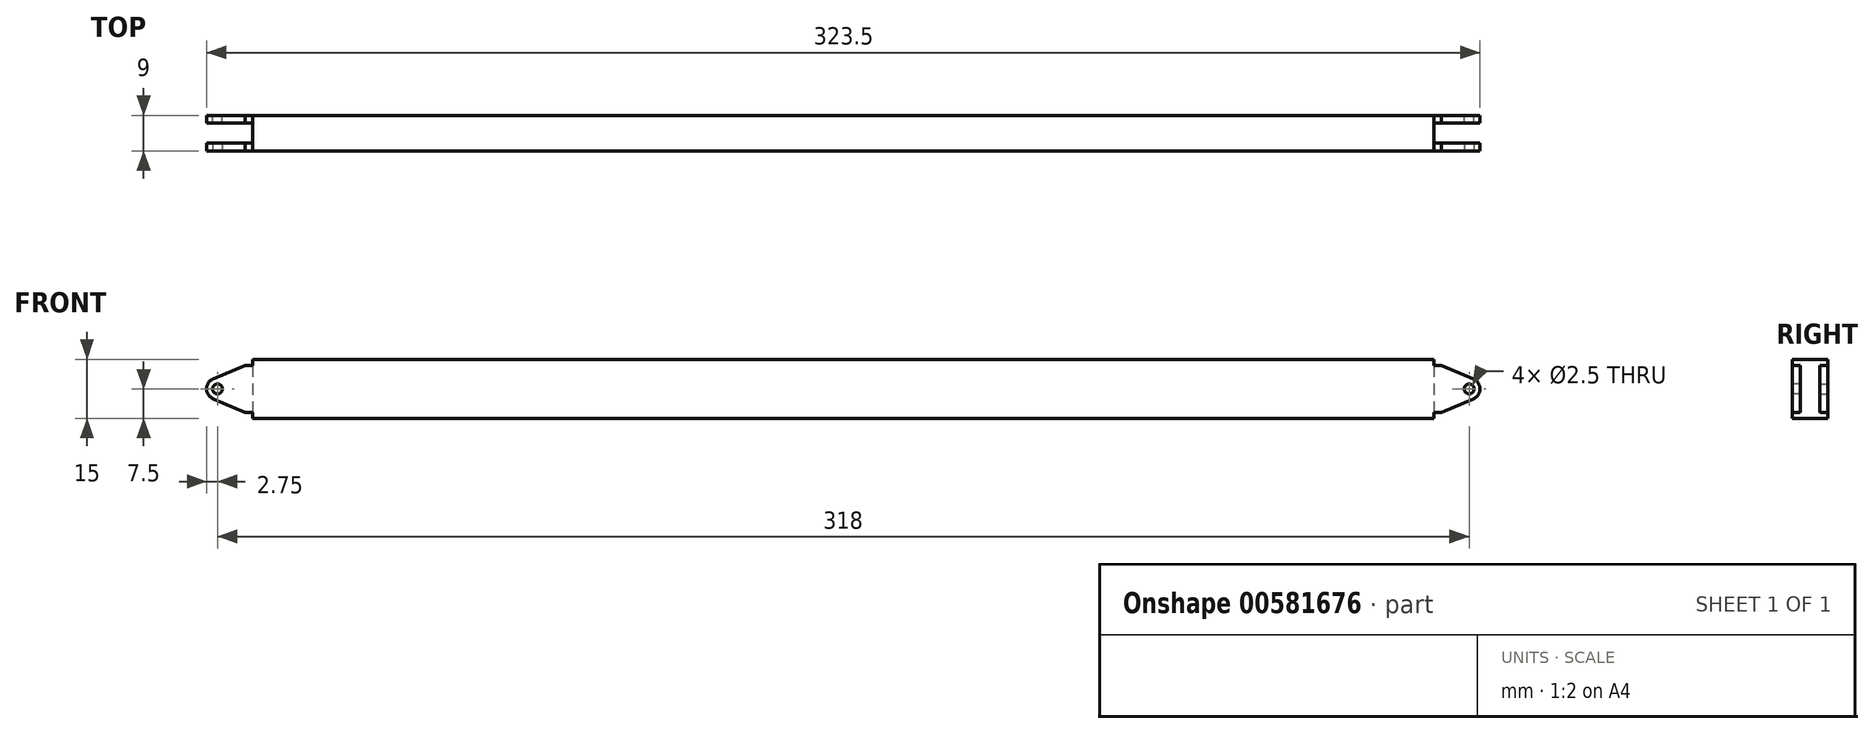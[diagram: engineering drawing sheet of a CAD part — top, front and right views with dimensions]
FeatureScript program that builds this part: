
annotation { "Feature Type Name" : "Feature", "Feature Type Description" : "" }
export const myFeature = defineFeature(function(context is Context, id is Id, definition is map)
    precondition{}
    {
        {
            var Q0;
            Q0=qCreatedBy(makeId("Front.planeOp"),FACE);
            var sketch = newSketch(context, id + "F0", { "sketchPlane" : qUnion([Q0])});
            skLineSegment(sketch, "E0.bottom", {"start": v(-150, 7.5) * mm, "end": v(150, 7.5) * mm});
            skLineSegment(sketch, "E0.top", {"start": v(-150, -7.5) * mm, "end": v(150, -7.5) * mm});
            skLineSegment(sketch, "E0.left", {"start": v(-150, 7.5) * mm, "end": v(-150, -7.5) * mm});
            skLineSegment(sketch, "E0.right", {"start": v(150, 7.5) * mm, "end": v(150, -7.5) * mm});
            skSolve(sketch);
        }
        {
            var Q0;
            Q0 = qSketchRegion(id + "F0", true);
            extrude(context, id + "F1", {"entities" : qUnion([Q0]), "depth" : 3 * mm, "offsetDistance" : 25 * mm});
        }
        {
            var Q0;
            Q0 = qSketchRegion(id + "F0", true);
            extrude(context, id + "F2", {"entities" : qUnion([Q0]), "operationType" : NewBodyOperationType.ADD, "oppositeDirection" : true, "depth" : 6 * mm, "offsetDistance" : 25 * mm});
        }
        {
            var Q0;
            Q0=makeQuery(id+"F1.opExtrude","CAP_FACE",FACE,{"disambiguationData":[OSD([sQuery(id+"F0.wireOp",EDGE,"E0.bottom"),sQuery(id+"F0.wireOp",EDGE,"E0.top"),sQuery(id+"F0.wireOp",EDGE,"E0.left"),sQuery(id+"F0.wireOp",EDGE,"E0.right")])],"isStart":false});
            var sketch = newSketch(context, id + "F3", { "sketchPlane" : qUnion([Q0])});
            skCircle(sketch, "E1", {"center": v(159, 0) * mm, "radius": 1.25 * mm});
            skCircle(sketch, "E2", {"center": v(159, 0) * mm, "radius": 2.75 * mm});
            skLineSegment(sketch, "E3.bottom", {"start": v(150, -6) * mm, "end": v(152, -6) * mm});
            skLineSegment(sketch, "E3.top", {"start": v(150, 6) * mm, "end": v(152, 6) * mm});
            skLineSegment(sketch, "E3.left", {"start": v(150, -6) * mm, "end": v(150, 6) * mm});
            skLineSegment(sketch, "E3.right", {"start": v(152, -6) * mm, "end": v(152, 6) * mm});
            skLineSegment(sketch, "E4", {"start": v(152, -6) * mm, "end": v(160.09, -2.53) * mm});
            skLineSegment(sketch, "E5", {"start": v(152, 6) * mm, "end": v(160.09, 2.53) * mm});
            skLineSegment(sketch, "E6.bottom", {"start": v(-150, 6) * mm, "end": v(-152, 6) * mm});
            skLineSegment(sketch, "E6.top", {"start": v(-150, -6) * mm, "end": v(-152, -6) * mm});
            skLineSegment(sketch, "E6.left", {"start": v(-150, 6) * mm, "end": v(-150, -6) * mm});
            skLineSegment(sketch, "E6.right", {"start": v(-152, 6) * mm, "end": v(-152, -6) * mm});
            skCircle(sketch, "E7", {"center": v(-159, 0) * mm, "radius": 1.25 * mm});
            skCircle(sketch, "E8", {"center": v(-159, 0) * mm, "radius": 2.75 * mm});
            skLineSegment(sketch, "E9", {"start": v(-152, 6) * mm, "end": v(-160.09, 2.53) * mm});
            skLineSegment(sketch, "E10", {"start": v(-152, -6) * mm, "end": v(-160.09, -2.53) * mm});
            skSolve(sketch);
        }
        {
            var Q0;
            Q0=makeQuery(id+"F2.opExtrude","CAP_FACE",FACE,{"disambiguationData":[OSD([sQuery(id+"F0.wireOp",EDGE,"E0.bottom"),sQuery(id+"F0.wireOp",EDGE,"E0.top"),sQuery(id+"F0.wireOp",EDGE,"E0.left"),sQuery(id+"F0.wireOp",EDGE,"E0.right")])],"isStart":false});
            var sketch = newSketch(context, id + "F4", { "sketchPlane" : qUnion([Q0])});
            skCircle(sketch, "E11", {"center": v(159, 0) * mm, "radius": 1.25 * mm});
            skCircle(sketch, "E12", {"center": v(159, 0) * mm, "radius": 2.75 * mm});
            skLineSegment(sketch, "E13.bottom", {"start": v(150, -6) * mm, "end": v(152, -6) * mm});
            skLineSegment(sketch, "E13.top", {"start": v(150, 6) * mm, "end": v(152, 6) * mm});
            skLineSegment(sketch, "E13.left", {"start": v(150, -6) * mm, "end": v(150, 6) * mm});
            skLineSegment(sketch, "E13.right", {"start": v(152, -6) * mm, "end": v(152, 6) * mm});
            skLineSegment(sketch, "E14", {"start": v(152, -6) * mm, "end": v(160.09, -2.53) * mm});
            skLineSegment(sketch, "E15", {"start": v(152, 6) * mm, "end": v(160.09, 2.53) * mm});
            skLineSegment(sketch, "E16.bottom", {"start": v(-150, 6) * mm, "end": v(-152, 6) * mm});
            skLineSegment(sketch, "E16.top", {"start": v(-150, -6) * mm, "end": v(-152, -6) * mm});
            skLineSegment(sketch, "E16.left", {"start": v(-150, 6) * mm, "end": v(-150, -6) * mm});
            skLineSegment(sketch, "E16.right", {"start": v(-152, 6) * mm, "end": v(-152, -6) * mm});
            skCircle(sketch, "E17", {"center": v(-159, 0) * mm, "radius": 1.25 * mm});
            skCircle(sketch, "E18", {"center": v(-159, 0) * mm, "radius": 2.75 * mm});
            skLineSegment(sketch, "E19", {"start": v(-152, 6) * mm, "end": v(-160.09, 2.53) * mm});
            skLineSegment(sketch, "E20", {"start": v(-152, -6) * mm, "end": v(-160.09, -2.53) * mm});
            skSolve(sketch);
        }
        {
            var Q0;
            Q0=makeQuery(id+"F3.imprint","IMPRINT",FACE,{"disambiguationData":[TD([[makeQuery(id+"F3.imprint","IMPRINT",EDGE,{"derivedFrom":sQuery(id+"F3.wireOp",EDGE,"E7")}),-1.0]])]});
            var Q1;
            Q1=makeQuery(id+"F3.imprint","IMPRINT",FACE,{"disambiguationData":[TD([[makeQuery(id+"F3.imprint","IMPRINT",EDGE,{"derivedFrom":sQuery(id+"F3.wireOp",EDGE,"E6.right")}),-1.0]])]});
            var Q2;
            Q2=makeQuery(id+"F3.imprint","IMPRINT",FACE,{"disambiguationData":[TD([[makeQuery(id+"F3.imprint","IMPRINT",EDGE,{"derivedFrom":sQuery(id+"F3.wireOp",EDGE,"E6.bottom")}),1.0]])]});
            var Q3;
            Q3=makeQuery(id+"F3.imprint","IMPRINT",FACE,{"disambiguationData":[TD([[makeQuery(id+"F3.imprint","IMPRINT",EDGE,{"derivedFrom":sQuery(id+"F3.wireOp",EDGE,"E3.bottom")}),1.0]])]});
            var Q4;
            Q4=makeQuery(id+"F3.imprint","IMPRINT",FACE,{"disambiguationData":[TD([[makeQuery(id+"F3.imprint","IMPRINT",EDGE,{"derivedFrom":sQuery(id+"F3.wireOp",EDGE,"E3.right")}),-1.0]])]});
            var Q5;
            Q5=makeQuery(id+"F3.imprint","IMPRINT",FACE,{"disambiguationData":[TD([[makeQuery(id+"F3.imprint","IMPRINT",EDGE,{"derivedFrom":sQuery(id+"F3.wireOp",EDGE,"E1")}),-1.0]])]});
            extrude(context, id + "F5", {"entities" : qUnion([Q0, Q1, Q2, Q3, Q4, Q5]), "operationType" : NewBodyOperationType.ADD, "oppositeDirection" : true, "depth" : 2 * mm, "offsetDistance" : 25 * mm});
        }
        {
            var Q0;
            Q0=makeQuery(id+"F4.imprint","IMPRINT",FACE,{"disambiguationData":[TD([[makeQuery(id+"F4.imprint","IMPRINT",EDGE,{"derivedFrom":sQuery(id+"F4.wireOp",EDGE,"E16.right")}),-1.0]])]});
            var Q1;
            Q1=makeQuery(id+"F4.imprint","IMPRINT",FACE,{"disambiguationData":[TD([[makeQuery(id+"F4.imprint","IMPRINT",EDGE,{"derivedFrom":sQuery(id+"F4.wireOp",EDGE,"E16.bottom")}),1.0]])]});
            var Q2;
            Q2=makeQuery(id+"F4.imprint","IMPRINT",FACE,{"disambiguationData":[TD([[makeQuery(id+"F4.imprint","IMPRINT",EDGE,{"derivedFrom":sQuery(id+"F4.wireOp",EDGE,"E17")}),-1.0]])]});
            var Q3;
            Q3=makeQuery(id+"F4.imprint","IMPRINT",FACE,{"disambiguationData":[TD([[makeQuery(id+"F4.imprint","IMPRINT",EDGE,{"derivedFrom":sQuery(id+"F4.wireOp",EDGE,"E13.bottom")}),1.0]])]});
            var Q4;
            Q4=makeQuery(id+"F4.imprint","IMPRINT",FACE,{"disambiguationData":[TD([[makeQuery(id+"F4.imprint","IMPRINT",EDGE,{"derivedFrom":sQuery(id+"F4.wireOp",EDGE,"E13.right")}),-1.0]])]});
            var Q5;
            Q5=makeQuery(id+"F4.imprint","IMPRINT",FACE,{"disambiguationData":[TD([[makeQuery(id+"F4.imprint","IMPRINT",EDGE,{"derivedFrom":sQuery(id+"F4.wireOp",EDGE,"E11")}),-1.0]])]});
            extrude(context, id + "F6", {"entities" : qUnion([Q0, Q1, Q2, Q3, Q4, Q5]), "operationType" : NewBodyOperationType.ADD, "oppositeDirection" : true, "depth" : 2 * mm, "offsetDistance" : 25 * mm});
        }
    });
